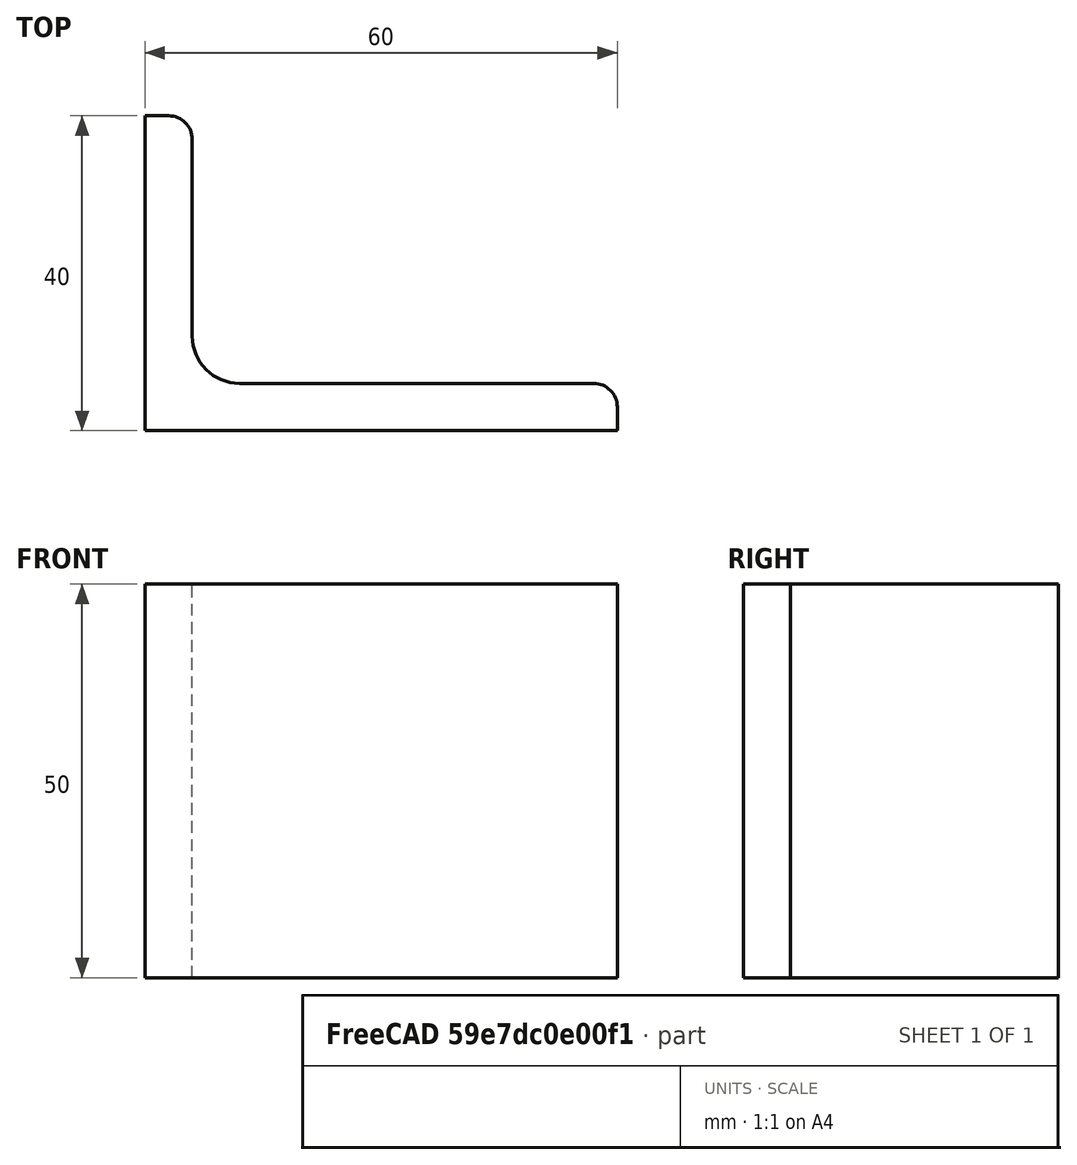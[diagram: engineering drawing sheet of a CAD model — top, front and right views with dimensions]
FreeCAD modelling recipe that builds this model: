
FCSTD DOCUMENT  (FreeCAD 0.15R4671 (Git))
Label: Angle Bar 60x40x6 EN10056 S235JR
License: All rights reserved
LicenseURL: http://en.wikipedia.org/wiki/All_rights_reserved
objects: Sketcher::SketchObject×1, Part::Extrusion×1
note: 2 computed .brp shape members not serialized (recipe doc carries the construction recipe); baked Part::Feature solids carry a one-line shape summary decoded from their .brp

FEATURE [Sketcher::SketchObject] Sketch
  sketch-geometry (9):
    g0: LineSegment StartX=0 StartY=0 StartZ=0 EndX=60 EndY=0 EndZ=0
    g1: LineSegment StartX=60 StartY=0 StartZ=0 EndX=60 EndY=3 EndZ=0
    g2: LineSegment StartX=57 StartY=6 StartZ=0 EndX=12 EndY=6 EndZ=0
    g3: LineSegment StartX=0 StartY=0 StartZ=0 EndX=0 EndY=40 EndZ=0
    g4: LineSegment StartX=0 StartY=40 StartZ=0 EndX=3 EndY=40 EndZ=0
    g5: LineSegment StartX=6 StartY=37 StartZ=0 EndX=6 EndY=12 EndZ=0
    g6: ArcOfCircle CenterX=12 CenterY=12 CenterZ=0 NormalX=0 NormalY=0 NormalZ=1 Radius=6 StartAngle=3.14159 EndAngle=4.71239
    g7: ArcOfCircle CenterX=3 CenterY=37 CenterZ=0 NormalX=0 NormalY=0 NormalZ=1 Radius=3 StartAngle=0 EndAngle=1.5708
    g8: ArcOfCircle CenterX=57 CenterY=3 CenterZ=0 NormalX=0 NormalY=0 NormalZ=1 Radius=3 StartAngle=0 EndAngle=1.5708
  constraints (23):
    c: Coincident(g0,g-1)
    c: Horizontal(g0)
    c: Coincident(g1,g0)
    c: Vertical(g1)
    c: Horizontal(g2)
    c: Coincident(g3,g-1)
    c: Vertical(g3)
    c: Coincident(g4,g3)
    c: Horizontal(g4)
    c: Vertical(g5)
    c: Tangent(g5,g6) = -1.5708
    c: Tangent(g2,g6) = 1.5708
    c: Tangent(g4,g7) = 1.5708
    c: Tangent(g5,g7) = 1.5708
    c: Tangent(g2,g8) = -1.5708
    c: Tangent(g1,g8) = -1.5708
    c: DistanceX(g0) = 60
    c: DistanceY(g3) = 40
    c: DistanceY(g0,g2) = 6
    c: DistanceX(g3,g5) = 6
    c: Radius(g6) = 6
    c: Radius(g8) = 3
    c: Radius(g7) = 3
FEATURE [Part::Extrusion] Extrude  label="Angle Bar 60x40x6 EN10056 S235JR"
  Base = -> Sketch
  Dir = (0,0,50)
  Solid = true
